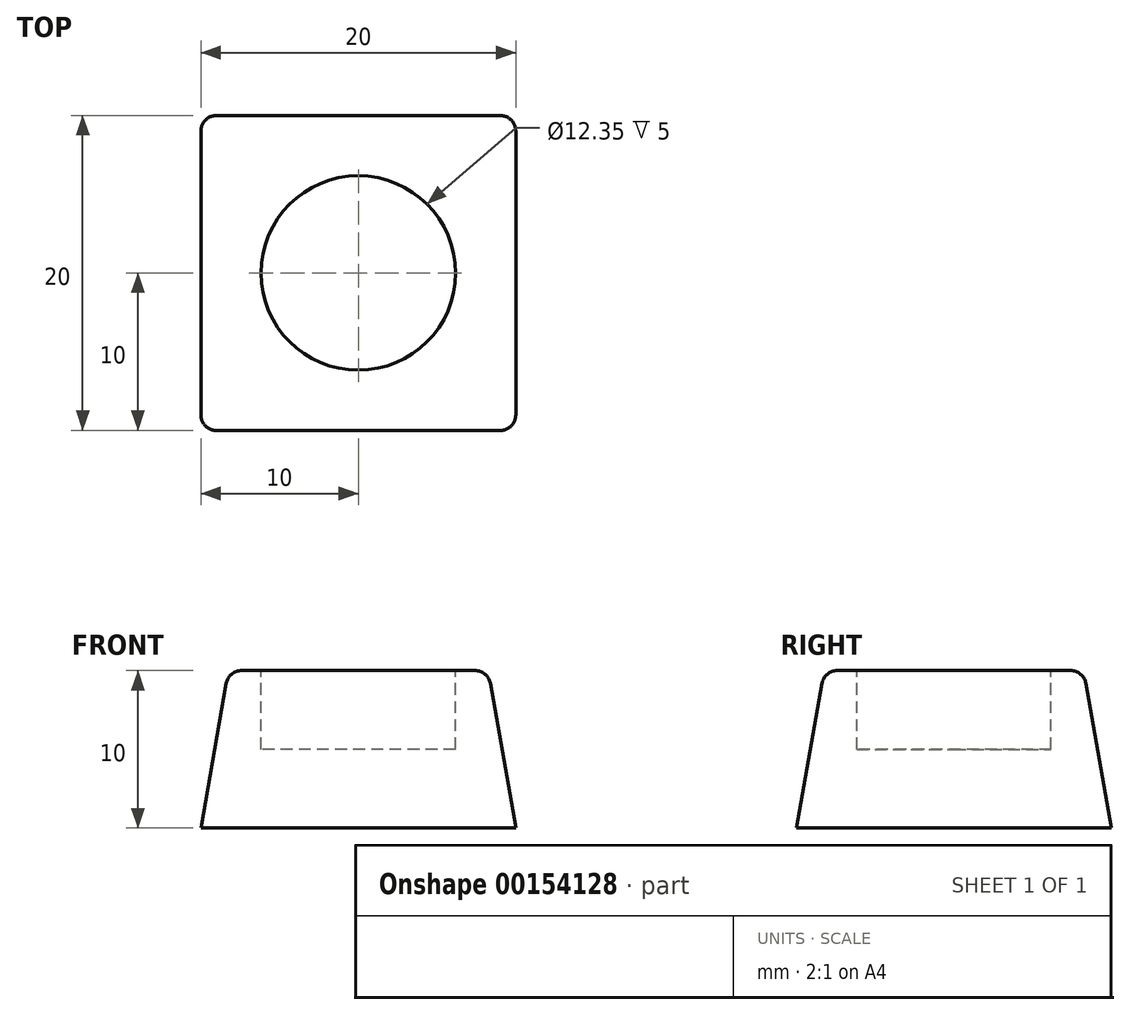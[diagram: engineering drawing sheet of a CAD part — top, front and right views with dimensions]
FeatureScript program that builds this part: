
annotation { "Feature Type Name" : "Feature", "Feature Type Description" : "" }
export const myFeature = defineFeature(function(context is Context, id is Id, definition is map)
    precondition{}
    {
        {
            var Q0;
            Q0=qCreatedBy(makeId("Top.planeOp"),FACE);
            var sketch = newSketch(context, id + "F0", { "sketchPlane" : qUnion([Q0])});
            skLineSegment(sketch, "E0.bottom", {"start": v(10, 10) * mm, "end": v(-10, 10) * mm});
            skLineSegment(sketch, "E0.top", {"start": v(10, -10) * mm, "end": v(-10, -10) * mm});
            skLineSegment(sketch, "E0.left", {"start": v(10, 10) * mm, "end": v(10, -10) * mm});
            skLineSegment(sketch, "E0.right", {"start": v(-10, 10) * mm, "end": v(-10, -10) * mm});
            skPoint(sketch, "E0.middle", {"position": v(0, 0) * mm});
            skSolve(sketch);
        }
        {
            var Q0;
            Q0 = qSketchRegion(id + "F0", true);
            extrude(context, id + "F1", {"entities" : qUnion([Q0]), "depth" : 10 * mm, "hasDraft" : true, "draftAngle" : 10 * degree, "draftPullDirection" : true});
        }
        {
            var Q0;
            Q0=makeQuery(id+"F1.opExtrude","CAP_FACE",FACE,{"disambiguationData":[OSD([sQuery(id+"F0.wireOp",EDGE,"E0.bottom"),sQuery(id+"F0.wireOp",EDGE,"E0.top"),sQuery(id+"F0.wireOp",EDGE,"E0.left"),sQuery(id+"F0.wireOp",EDGE,"E0.right")])],"isStart":false});
            var sketch = newSketch(context, id + "F2", { "sketchPlane" : qUnion([Q0])});
            skCircle(sketch, "E1", {"center": v(0, 0) * mm, "radius": 6.17 * mm});
            skSolve(sketch);
        }
        {
            var Q0;
            Q0=makeQuery(id+"F2.imprint","IMPRINT",FACE,{"disambiguationData":[TD([[makeQuery(id+"F2.imprint","IMPRINT",EDGE,{"derivedFrom":sQuery(id+"F2.wireOp",EDGE,"E1")}),1.0]])]});
            extrude(context, id + "F3", {"entities" : qUnion([Q0]), "operationType" : NewBodyOperationType.REMOVE, "oppositeDirection" : true, "depth" : 5 * mm});
        }
        {
            var Q0;
            Q0=makeQuery(id+"F1.opExtrude","SWEPT_EDGE",EDGE,{"disambiguationData":[OSD([sQuery(id+"F0.wireOp",EDGE,"E0.bottom"),sQuery(id+"F0.wireOp",EDGE,"E0.left")])]});
            var Q1;
            Q1=makeQuery(id+"F1.opExtrude","CAP_EDGE",EDGE,{"disambiguationData":[OSD([sQuery(id+"F0.wireOp",EDGE,"E0.bottom")])],"isStart":false});
            var Q2;
            Q2=makeQuery(id+"F1.opExtrude","CAP_EDGE",EDGE,{"disambiguationData":[OSD([sQuery(id+"F0.wireOp",EDGE,"E0.left")])],"isStart":false});
            var Q3;
            Q3=makeQuery(id+"F1.opExtrude","SWEPT_EDGE",EDGE,{"disambiguationData":[OSD([sQuery(id+"F0.wireOp",EDGE,"E0.bottom"),sQuery(id+"F0.wireOp",EDGE,"E0.right")])]});
            var Q4;
            Q4=makeQuery(id+"F1.opExtrude","CAP_EDGE",EDGE,{"disambiguationData":[OSD([sQuery(id+"F0.wireOp",EDGE,"E0.top")])],"isStart":false});
            var Q5;
            Q5=makeQuery(id+"F1.opExtrude","SWEPT_EDGE",EDGE,{"disambiguationData":[OSD([sQuery(id+"F0.wireOp",EDGE,"E0.top"),sQuery(id+"F0.wireOp",EDGE,"E0.left")])]});
            var Q6;
            Q6=makeQuery(id+"F1.opExtrude","SWEPT_EDGE",EDGE,{"disambiguationData":[OSD([sQuery(id+"F0.wireOp",EDGE,"E0.top"),sQuery(id+"F0.wireOp",EDGE,"E0.right")])]});
            var Q7;
            Q7=makeQuery(id+"F1.opExtrude","CAP_EDGE",EDGE,{"disambiguationData":[OSD([sQuery(id+"F0.wireOp",EDGE,"E0.right")])],"isStart":false});
            fillet(context, id + "F4", {"entities" : qUnion([Q0, Q1, Q2, Q3, Q4, Q5, Q6, Q7]), "radius" : 1 * mm, "tangentPropagation" : true, "allowEdgeOverflow" : false});
        }
    });
